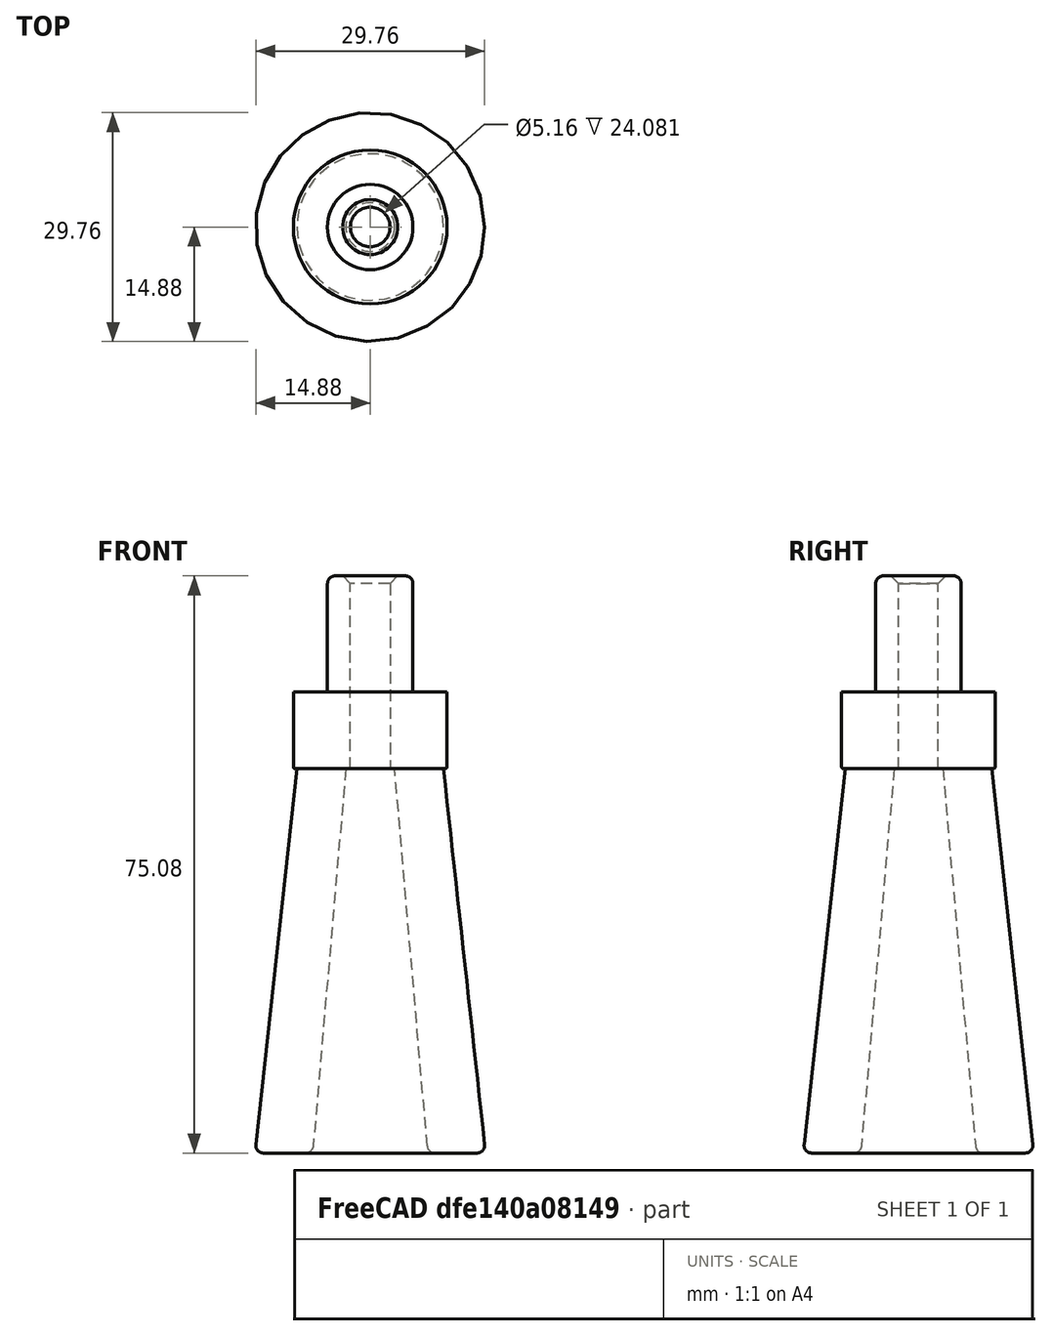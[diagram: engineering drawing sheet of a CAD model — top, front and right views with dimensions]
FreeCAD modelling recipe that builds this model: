
FCSTD DOCUMENT  (FreeCAD 0.19R24291 (Git))
Label: WorkBenchHandle_ForBnD
License: All rights reserved
LicenseURL: http://en.wikipedia.org/wiki/All_rights_reserved
objects: TechDraw::DrawViewDimension×7, PartDesign::Fillet×6, Sketcher::SketchObject×5, TechDraw::DrawProjGroupItem×4, PartDesign::Pad×2, PartDesign::AdditiveLoft×1, TechDraw::DrawSVGTemplate×1, PartDesign::Pocket×1, PartDesign::Chamfer×1, PartDesign::Body×1, TechDraw::DrawProjGroup×1, TechDraw::DrawPage×1
note: 28 computed .brp shape members not serialized (recipe doc carries the construction recipe); baked Part::Feature solids carry a one-line shape summary decoded from their .brp

FEATURE [Sketcher::SketchObject] Sketch
  FullyConstrained = true
  MapMode = 5
  Support = -> [XY_Plane]
  sketch-geometry (2):
    g0: Circle CenterX=0 CenterY=0 CenterZ=0 NormalX=0 NormalY=0 NormalZ=1 AngleXU=0 Radius=15
    g1: Circle CenterX=0 CenterY=0 CenterZ=0 NormalX=0 NormalY=0 NormalZ=1 AngleXU=0 Radius=7.5
  constraints (4):
    c: Coincident(g0,g-1)
    c: Coincident(g1,g0)
    c: Diameter(g0) = 30
    c: Diameter(g1) = 15
FEATURE [Sketcher::SketchObject] Sketch001
  AttachmentOffset = pos=(0,0,50) rot=(0,0,1;0rad)
  FullyConstrained = true
  MapMode = 5
  Placement = pos=(0,0,50) rot=(0,0,1;0rad)
  Support = -> [XY_Plane]
  sketch-geometry (2):
    g0: Circle CenterX=0 CenterY=0 CenterZ=0 NormalX=0 NormalY=0 NormalZ=1 AngleXU=0 Radius=9.525
    g1: Circle CenterX=0 CenterY=0 CenterZ=0 NormalX=0 NormalY=0 NormalZ=1 AngleXU=0 Radius=3.175
  constraints (4):
    c: Coincident(g0,g-1)
    c: Coincident(g1,g0)
    c: Diameter(g0) = 19.05
    c: Diameter(g1) = 6.35
FEATURE [PartDesign::AdditiveLoft] AdditiveLoft  label="AdditiveLoftHandel"
  Closed = false
  Profile = -> Sketch
  Ruled = false
  Sections = -> [Sketch001]
FEATURE [Sketcher::SketchObject] Sketch002
  FullyConstrained = true
  MapMode = 5
  Placement = pos=(0,0,50) rot=(0,0,1;0rad)
  Support = -> [AdditiveLoft]
  sketch-geometry (1):
    g0: Circle CenterX=0 CenterY=0 CenterZ=0 NormalX=0 NormalY=0 NormalZ=1 AngleXU=0 Radius=10
  constraints (2):
    c: Coincident(g0,g-1)
    c: Diameter(g0) = 20
FEATURE [PartDesign::Pad] Pad  label="PadBoss"
  BaseFeature = -> AdditiveLoft
  Direction = (1,1,1)
  Length = 10
  Length2 = 100
  Profile = -> Sketch002
  Type = 0
FEATURE [TechDraw::DrawSVGTemplate] Template
  EditableTexts = Approved1=Approved 1; Approved2=Approved 2; CheckedBy=on 20230709; Code=Code; CompanyAddress=3433 Ridgeway Trail; CompanyName=Amused Scientist; DrawingNumber=Drawing Number; DrawingTitle1=WorkBenchHandle For BnD; DrawingTitle2=Drawing Title 2; DrawingTitle3=Drawing Title 3; DrawnBy=(Forrest) Lee Erickson; Revision=Rev; Scale=Scale 1:1; Sheet=Sheet n of m
  Height = 215.9
  Orientation = 1
  Width = 279.4
FEATURE [Sketcher::SketchObject] Sketch004
  FullyConstrained = true
  MapMode = 5
  Placement = pos=(0,0,60) rot=(0,0,1;0rad)
  sketch-geometry (1):
    g0: Circle CenterX=0 CenterY=0 CenterZ=0 NormalX=0 NormalY=0 NormalZ=1 AngleXU=0 Radius=5.55625
  constraints (2):
    c: Coincident(g0,g-1)
    c: Diameter(g0) = 11.1125
FEATURE [PartDesign::Pad] Pad001  label="PadPinIntoCrank"
  BaseFeature = -> Pad
  Direction = (1,1,1)
  Length = 15.0813
  Length2 = 100.076
  Profile = -> Sketch004
  Type = 0
FEATURE [Sketcher::SketchObject] Sketch005
  FullyConstrained = true
  MapMode = 5
  Placement = pos=(0,0,75.0812) rot=(0,0,1;0rad)
  Support = -> [Pad001]
  sketch-geometry (1):
    g0: Circle CenterX=0 CenterY=0 CenterZ=0 NormalX=0 NormalY=0 NormalZ=1 AngleXU=0 Radius=2.57969
  constraints (2):
    c: Coincident(g0,g-1)
    c: Diameter(g0) = 5.15937
FEATURE [PartDesign::Pocket] Pocket001  label="PocketBolt"
  BaseFeature = -> Pad001
  Length = 5.08
  Length2 = 100.076
  Profile = -> Sketch005
  Type = 1
FEATURE [PartDesign::Fillet] Fillet
  Base = -> Pad001 [Edge6,Edge10]
  BaseFeature = -> Pad001
  Radius = 0.999998
  SupportTransform = false
FEATURE [PartDesign::Fillet] Fillet001
  Base = -> Fillet [Edge16]
  BaseFeature = -> Fillet
  Radius = 0.999998
  SupportTransform = false
FEATURE [PartDesign::Fillet] Fillet002
  Base = -> Fillet001 [Edge8]
  BaseFeature = -> Fillet001
  Radius = 0.254
  SupportTransform = false
FEATURE [PartDesign::Chamfer] Chamfer
  Angle = 45
  Base = -> Pocket001 [Edge11]
  BaseFeature = -> Pocket001
  ChamferType = 0
  FlipDirection = false
  Size = 1
  Size2 = 1
  SupportTransform = false
FEATURE [PartDesign::Fillet] Fillet003
  Base = -> Chamfer [Edge16,Edge13]
  BaseFeature = -> Chamfer
  Radius = 0.999998
  SupportTransform = false
FEATURE [PartDesign::Fillet] Fillet004
  Base = -> Fillet003 [Edge16]
  BaseFeature = -> Fillet003
  Radius = 0.999998
  SupportTransform = false
FEATURE [PartDesign::Fillet] Fillet005
  Base = -> Fillet004 [Edge14]
  BaseFeature = -> Fillet004
  Radius = 0.254
  SupportTransform = false
FEATURE [PartDesign::Body] Body
  Group = -> [Sketch,Sketch001,AdditiveLoft,Sketch002,Pad,Sketch004,Pad001,Sketch005,Pocket001,Fillet,Fillet001,Fillet002,Chamfer,Fillet003,Fillet004,Fillet005]
  Origin = -> Origin
  Tip = -> Fillet005
FEATURE [TechDraw::DrawProjGroupItem] ProjItem004  label="Front001"
  CoarseView = false
  Direction = (1,0,0)
  Focus = 100
  HardHidden = false
  IsoCount = 0
  IsoHidden = false
  IsoVisible = false
  LockPosition = true
  Perspective = false
  Rotation = 0
  RotationVector = (0,0,1)
  ScaleType = 2
  SeamHidden = false
  SeamVisible = false
  SmoothHidden = false
  SmoothVisible = false
  Source = -> [Body]
  Type = 0
  X = 0
  XDirection = (0,0,1)
  Y = 0
FEATURE [TechDraw::DrawProjGroupItem] ProjItem005  label="FrontBottomLeft001"
  CoarseView = false
  Direction = (0.57735,0.57735,-0.57735)
  Focus = 100
  HardHidden = false
  IsoCount = 0
  IsoHidden = false
  IsoVisible = false
  LockPosition = true
  Perspective = false
  Rotation = 0
  RotationVector = (1,0,0)
  ScaleType = 2
  SeamHidden = false
  SeamVisible = false
  SmoothHidden = false
  SmoothVisible = false
  Source = -> [Body]
  Type = 8
  X = 90.1975
  XDirection = (0.707107,0,0.707107)
  Y = 67.4708
FEATURE [TechDraw::DrawProjGroupItem] ProjItem006  label="Right001"
  CoarseView = false
  Direction = (1e-16,0,1)
  Focus = 100
  HardHidden = false
  IsoCount = 0
  IsoHidden = false
  IsoVisible = false
  LockPosition = true
  Perspective = false
  Rotation = 0
  RotationVector = (1,0,0)
  ScaleType = 2
  SeamHidden = false
  SeamVisible = false
  SmoothHidden = false
  SmoothVisible = false
  Source = -> [Body]
  Type = 2
  X = -69.895
  XDirection = (-1,0,1e-16)
  Y = 0
FEATURE [TechDraw::DrawProjGroupItem] ProjItem007  label="FrontBottomRight001"
  CoarseView = false
  Direction = (0.57735,0.57735,0.57735)
  Focus = 100
  HardHidden = false
  IsoCount = 0
  IsoHidden = false
  IsoVisible = false
  LockPosition = true
  Perspective = false
  Rotation = 0
  RotationVector = (1,0,0)
  ScaleType = 2
  SeamHidden = false
  SeamVisible = false
  SmoothHidden = false
  SmoothVisible = false
  Source = -> [Body]
  Type = 9
  X = -5.79715
  XDirection = (-0.707107,0,0.707107)
  Y = 61.3243
FEATURE [TechDraw::DrawProjGroup] ProjGroup001  label="ProjGroup"
  Anchor = -> ProjItem004
  AutoDistribute = true
  LockPosition = false
  ProjectionType = 0
  Rotation = 0
  ScaleType = 0
  Source = -> [Body]
  Views = -> [ProjItem004,ProjItem005,ProjItem006,ProjItem007]
  X = 120.351
  Y = 96.2835
  spacingX = 15
  spacingY = 15
FEATURE [TechDraw::DrawViewDimension] Dimension015
  Arbitrary = false
  ArbitraryTolerances = false
  EqualTolerance = true
  FormatSpec = %.2f
  FormatSpecOverTolerance = %+.2f
  FormatSpecUnderTolerance = %+.2f
  Inverted = false
  LockPosition = false
  MeasureType = 1
  OverTolerance = 0
  References2D = -> [ProjItem004]
  Rotation = 0
  ScaleType = 0
  TheoreticalExact = false
  Type = 1
  UnderTolerance = 0
  X = 54.4201
  Y = 27.9743
FEATURE [TechDraw::DrawViewDimension] Dimension016
  Arbitrary = false
  ArbitraryTolerances = false
  EqualTolerance = true
  FormatSpec = %.2f
  FormatSpecOverTolerance = %+.2f
  FormatSpecUnderTolerance = %+.2f
  Inverted = false
  LockPosition = false
  MeasureType = 1
  OverTolerance = 0
  References2D = -> [ProjItem004]
  Rotation = 0
  ScaleType = 0
  TheoreticalExact = false
  Type = 1
  UnderTolerance = 0
  X = -8.16284
  Y = 33.2673
FEATURE [TechDraw::DrawViewDimension] Dimension
  Arbitrary = false
  ArbitraryTolerances = false
  EqualTolerance = true
  FormatSpec = %.2f
  FormatSpecOverTolerance = %+.2f
  FormatSpecUnderTolerance = %+.2f
  Inverted = false
  LockPosition = false
  MeasureType = 1
  OverTolerance = 0
  References2D = -> [ProjItem004]
  Rotation = 0
  ScaleType = 0
  TheoreticalExact = false
  Type = 1
  UnderTolerance = 0
  X = 51.2025
  Y = -8.4129
FEATURE [TechDraw::DrawViewDimension] Dimension018
  Arbitrary = false
  ArbitraryTolerances = false
  EqualTolerance = true
  FormatSpec = %.2f
  FormatSpecOverTolerance = %+.2f
  FormatSpecUnderTolerance = %+.2f
  Inverted = false
  LockPosition = false
  MeasureType = 1
  OverTolerance = 0
  References2D = -> [ProjItem004]
  Rotation = 0
  ScaleType = 0
  TheoreticalExact = false
  Type = 2
  UnderTolerance = 0
  X = 96.8398
  Y = 20.9124
FEATURE [TechDraw::DrawViewDimension] Dimension019
  Arbitrary = false
  ArbitraryTolerances = false
  EqualTolerance = true
  FormatSpec = %.2f
  FormatSpecOverTolerance = %+.2f
  FormatSpecUnderTolerance = %+.2f
  Inverted = false
  LockPosition = false
  MeasureType = 1
  OverTolerance = 0
  References2D = -> [ProjItem004]
  Rotation = 0
  ScaleType = 0
  TheoreticalExact = false
  Type = 2
  UnderTolerance = 0
  X = 74.0517
  Y = 21.237
FEATURE [TechDraw::DrawViewDimension] Dimension020
  Arbitrary = false
  ArbitraryTolerances = false
  EqualTolerance = true
  FormatSpec = %.2f
  FormatSpecOverTolerance = %+.2f
  FormatSpecUnderTolerance = %+.2f
  Inverted = false
  LockPosition = false
  MeasureType = 1
  OverTolerance = 0
  References2D = -> [ProjItem004]
  Rotation = 0
  ScaleType = 0
  TheoreticalExact = false
  Type = 1
  UnderTolerance = 0
  X = 0.617911
  Y = -21.0572
FEATURE [TechDraw::DrawViewDimension] Dimension021
  Arbitrary = false
  ArbitraryTolerances = false
  EqualTolerance = true
  FormatSpec = %.2f
  FormatSpecOverTolerance = %+.2f
  FormatSpecUnderTolerance = %+.2f
  Inverted = false
  LockPosition = false
  MeasureType = 1
  OverTolerance = 0
  References2D = -> [ProjItem004]
  Rotation = 0
  ScaleType = 0
  TheoreticalExact = false
  Type = 2
  UnderTolerance = 0
  X = 85.2766
  Y = 23.4039
FEATURE [TechDraw::DrawPage] Page  label="PageHandel"
  KeepUpdated = true
  NextBalloonIndex = 1
  ProjectionType = 0
  Template = -> Template
  Views = -> [ProjGroup001,Dimension015,Dimension016,Dimension,Dimension018,Dimension019,Dimension020,Dimension021]
